# Revit family: Building-ContenitoriParete-GEWISS-40CDK-CENTRALINI_IP65_2X
name_source: partatom
category: Apparecchi elettrici
revit_build: Autodesk Revit 2016 (Build: 20161004_0715(x64)
units: mm (PartAtom-declared; Revit-internal decimal feet)

## family parameters
Condiviso = No
Host = Superficie
Mantenere orientamento annotazione = Sì
Numero OmniClass = 23.80.30.11.17
Punto di calcolo locali = Sì
Quota connettore circolare = Usa diametro
Taglio con vuoti quando caricato = No
Tipo di parte = Normale
Titolo OmniClass = Distribution Boards and Control Panels

## types (2) — shared parameters
Accessori per ripristino isolamento = Tappi coprivite (GW44623) o staffe di fissaggio in resina (GW44621)
Catalogo = BUILDING
Catalogo Serie = 40 CDK
Classe isolamento = II (secondo Norma IEC 61140)
Codice Electrocod = 0321
Colore = Grigio RAL 7035
Colore porta = Trasparente fume'
Corrente nominale: = 125A
Diametro_tubazione = 30 mm  [stored 0.0984252 ft]
Dimensione_modulo = 18 mm  [stored 0.0590551 ft]
Glow Wire Test = 650°C
Grado di protezione = IP65
H_finestratura = 45 mm  [stored 0.147638 ft]
H_quadro = 463 mm  [stored 1.51903 ft]
IDF = 9199d71a-6e6e-4f8a-8deb-20131af3a072
IDT = 3c4ae22a-7553-4dc5-ae30-2fcf832f6236
L_finestratura = 324 mm  [stored 1.06299 ft]
L_quadro = 410 mm  [stored 1.34514 ft]
N.M. = 18
Norma di riferimento = EN 60670-1 (CEI 23-48) IEC60670-24 CEI 23-49
Normativa = EN 60670-1 (CEI 23-48) IEC60670-24 CEI 23-49
Produttore = GEWISS S.p.A.
Prondita_quadro = 140 mm  [stored 0.459318 ft]
Prospetto di default = 1219 mm
QUADRO = FINITURA BIANCA
Resistenza agli urti = IK09
SEO = Quadro
Scheda Tecnica = https://www.gewiss.com
Spostamento_x_ET = 1000 mm  [stored 3.28084 ft]
Temperatura di impiego = -25 +60 °C
Tensione di isolamento: = 1000 V secondo EN 62208 sia in ac che in dc
Tensione nominale = 400V
Tensione nominale di isolamento (Ui) = 1000 V
Termopressione con biglia = 70 °C
Tipo Materiale = Halogen free secondo norma EN 60754-2
URL = https://www.gewiss.com
Versione file RFA = 18.0
fase1 = 0 VA
voltaggio_quadro = 0 V

## per-type parameters (varying)
| type | Codice EAN | Descrizione | Dim. esterne BxHxP (mm) | Max.morsettiere installabili | Modello | N. mod. EN 50022 | N. mod. EN 50022: | Potenza dissipabile (W) |
| GW40107 - QUADRO DIS.PARETE 36M.(18X2) IP65 | 8011564062221 | QUADRO DIS.PARETE 36M.(18X2) IP65 | 410x463x140 | 2 x18 moduli | GW40107 | 36 (18x2) | 36 (18x2) | 43 |
| GW40104 - QUADRO DIS.PARETE 24M.(12X2) IP65 | 8011564062207 | QUADRO DIS.PARETE 24M.(12X2) IP65 | 298x420x140 | 2 x 12 moduli | GW40104 | 24 | 24 (12X2) | 32 |

note: [stored X ft] marks values corroborated as IEEE doubles in the binary element streams (Revit-internal decimal feet)
